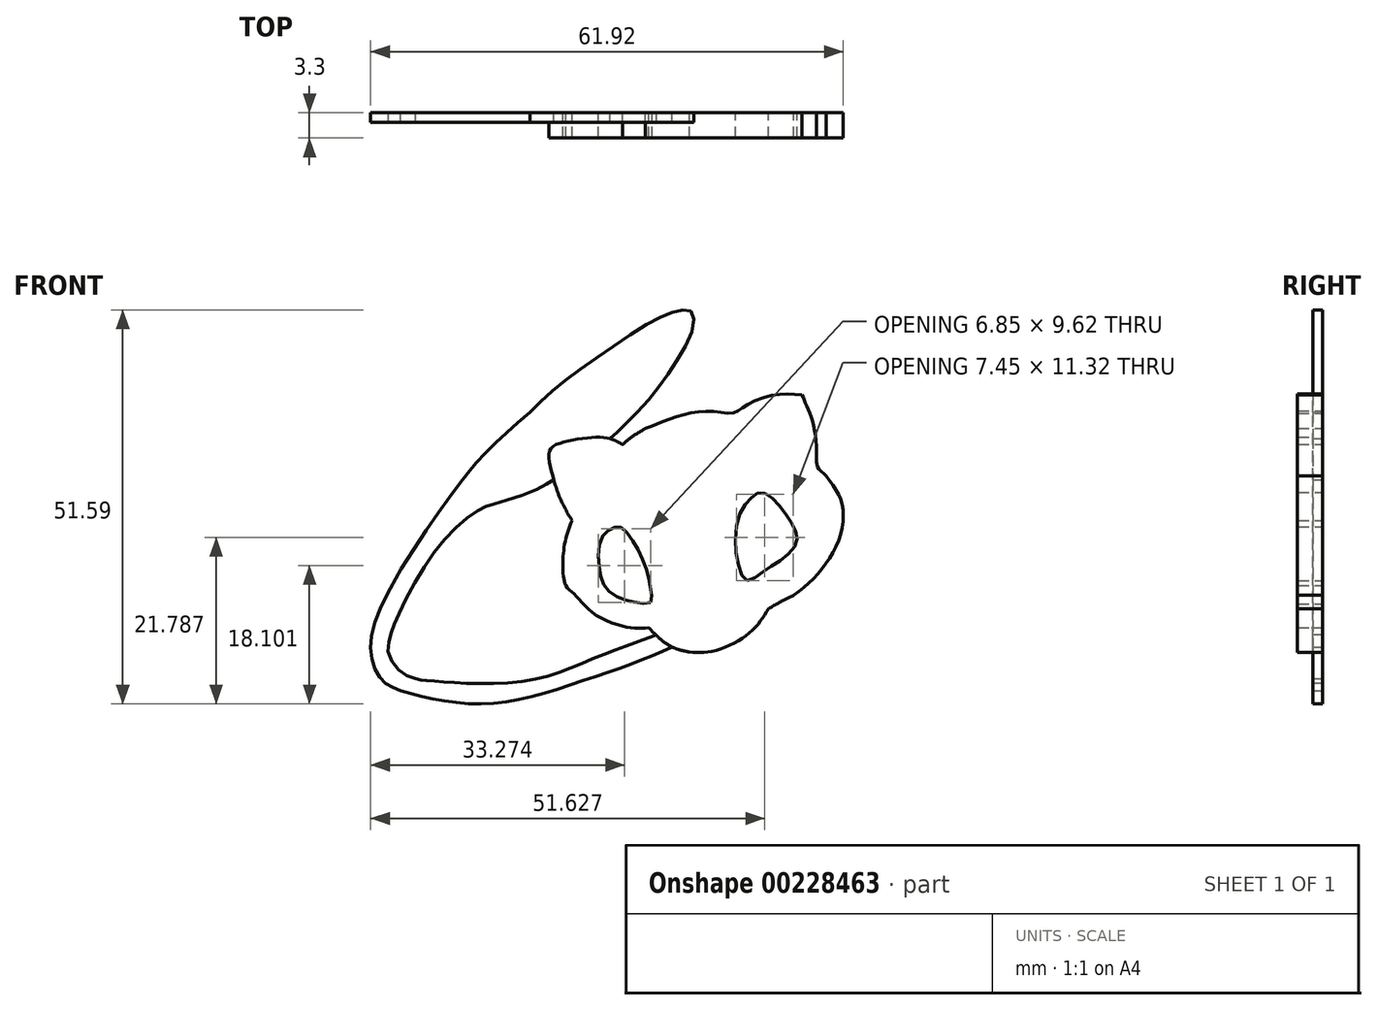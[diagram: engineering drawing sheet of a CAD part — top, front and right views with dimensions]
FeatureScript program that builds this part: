
annotation { "Feature Type Name" : "Feature", "Feature Type Description" : "" }
export const myFeature = defineFeature(function(context is Context, id is Id, definition is map)
    precondition{}
    {
        {
            var Q0;
            Q0=qCreatedBy(makeId("Front.planeOp"),FACE);
            var sketch = newSketch(context, id + "F0", { "sketchPlane" : qUnion([Q0])});
            skFitSpline(sketch, "E0", {"points": [v(-2.32, -20.69) * mm, v(0, -21.48) * mm, v(2.66, -21.63) * mm, v(5.5, -21.48) * mm, v(8.04, -20.05) * mm, v(10.01, -18.79) * mm], "startDerivative": vector(11.78, -4.97) * mm, "endDerivative": vector(10.2, 6.29) * mm});
            skFitSpline(sketch, "E1", {"points": [v(10.01, -18.79) * mm, v(12.15, -18.79) * mm, v(14.12, -18.79) * mm], "startDerivative": vector(4.23, 0) * mm, "endDerivative": vector(4, 0) * mm});
            skFitSpline(sketch, "E2", {"points": [v(14.12, -18.79) * mm, v(15.15, -21) * mm, v(16.42, -25.59) * mm, v(16.9, -29.38) * mm, v(17.13, -31.52) * mm], "startDerivative": vector(4.7, -9.02) * mm, "endDerivative": vector(1.16, -9.79) * mm});
            skFitSpline(sketch, "E3", {"points": [v(17.13, -31.52) * mm, v(17.74, -37.26) * mm, v(18.21, -42.48) * mm, v(19.24, -46.44) * mm, v(21.77, -48.9) * mm, v(26.22, -49.33) * mm, v(29.31, -47.38) * mm, v(29.8, -42.57) * mm, v(28.13, -36.9) * mm, v(26.29, -33.14) * mm, v(25.49, -31.52) * mm], "startDerivative": vector(5.72, -49.62) * mm, "endDerivative": vector(-10.88, 22.58) * mm});
            skFitSpline(sketch, "E4", {"points": [v(25.49, -31.52) * mm, v(24.09, -28.02) * mm, v(21.77, -21.94) * mm, v(20.2, -17.99) * mm, v(19.14, -16.04) * mm, v(18.38, -14.91) * mm], "startDerivative": vector(-6.12, 15.14) * mm, "endDerivative": vector(-5.8, 8.42) * mm});
            skFitSpline(sketch, "E5", {"points": [v(18.38, -14.91) * mm, v(18.1, -14.5) * mm], "startDerivative": vector(-0.29, 0.4) * mm, "endDerivative": vector(-0.29, 0.4) * mm});
            skFitSpline(sketch, "E6", {"points": [v(18.1, -14.5) * mm, v(18.1, -13.28) * mm, v(17.88, -10.97) * mm, v(16.93, -7.62) * mm, v(15.89, -5.67) * mm, v(14.88, -4.05) * mm], "startDerivative": vector(0.1, 7.63) * mm, "endDerivative": vector(-5.4, 8.63) * mm});
            skFitSpline(sketch, "E7", {"points": [v(14.88, -4.05) * mm, v(11.85, -1.17) * mm, v(8.44, 1.46) * mm, v(5.98, 3.57) * mm, v(4.78, 4.43) * mm, v(3.98, 5.1) * mm], "startDerivative": vector(-11.6, 11.83) * mm, "endDerivative": vector(-6.16, 5.39) * mm});
            skFitSpline(sketch, "E8", {"points": [v(3.98, 5.1) * mm, v(2.84, 6.42) * mm, v(1.91, 7.69) * mm, v(1.76, 8.46) * mm, v(1.71, 9.21) * mm, v(3.26, 9.37) * mm, v(5.98, 9.4) * mm, v(8.14, 9.24) * mm, v(9.13, 9.26) * mm, v(10.44, 8.7) * mm, v(11.35, 8.75) * mm, v(11.94, 9.66) * mm, v(12.76, 10.03) * mm, v(13.72, 10.65) * mm, v(13.36, 11.47) * mm, v(12.63, 11.98) * mm, v(12.7, 12.51) * mm], "startDerivative": vector(-14.72, 17.32) * mm, "endDerivative": vector(5.26, 13.9) * mm});
            skFitSpline(sketch, "E9", {"points": [v(12.7, 12.51) * mm, v(12.98, 13.02) * mm, v(12.4, 13.47) * mm, v(10.15, 14.02) * mm, v(7.27, 14.48) * mm, v(3.98, 14.64) * mm, v(2.38, 14.68) * mm], "startDerivative": vector(4.65, 5.52) * mm, "endDerivative": vector(-9, 0.23) * mm});
            skFitSpline(sketch, "E10", {"points": [v(2.38, 14.68) * mm, v(0, 14.68) * mm, v(-1.76, 14.68) * mm, v(-2.48, 15.55) * mm, v(-3.52, 16.92) * mm], "startDerivative": vector(-8.12, 0.34) * mm, "endDerivative": vector(-4.58, 5.53) * mm});
            skFitSpline(sketch, "E11", {"points": [v(-2.32, -20.69) * mm, v(-3.79, -21.48) * mm, v(-5.4, -21.63) * mm, v(-6.07, -21.63) * mm, v(-6.03, -22.06) * mm, v(-5.56, -23.59) * mm, v(-5.05, -24.67) * mm, v(-4.48, -25.94) * mm, v(-4.34, -26.18) * mm], "startDerivative": vector(-8.76, -5.85) * mm, "endDerivative": vector(1.87, -2.8) * mm});
            skFitSpline(sketch, "E12", {"points": [v(-4.34, -26.18) * mm, v(-3.52, -27.98) * mm, v(-2.32, -30.61) * mm, v(-1.07, -32.7) * mm, v(-0.47, -35.15) * mm, v(-0.51, -37.64) * mm, v(-1.62, -39.82) * mm, v(-3.52, -40.79) * mm, v(-6.34, -39.72) * mm, v(-9.34, -35.24) * mm, v(-10.78, -31.58) * mm, v(-12.12, -26.18) * mm, v(-12.77, -21.63) * mm, v(-13.04, -17.99) * mm, v(-12.9, -15.54) * mm], "startDerivative": vector(14.12, -29.7) * mm, "endDerivative": vector(3.47, 37.06) * mm});
            skFitSpline(sketch, "E13", {"points": [v(-12.9, -15.54) * mm, v(-11.8, -17.77) * mm, v(-9.63, -20.05) * mm, v(-8.07, -20.89) * mm, v(-6.86, -21.34) * mm, v(-6.07, -21.63) * mm], "startDerivative": vector(3.79, -9.41) * mm, "endDerivative": vector(5.46, -2.04) * mm});
            skFitSpline(sketch, "E14", {"points": [v(-12.9, -15.54) * mm, v(-12.9, -11.74) * mm, v(-11.8, -7.19) * mm, v(-10.92, -5.89) * mm, v(-10.92, -5.86) * mm], "startDerivative": vector(-0.49, 10.24) * mm, "endDerivative": vector(-0.26, 0.72) * mm});
            skFitSpline(sketch, "E15", {"points": [v(-10.92, -5.87) * mm, v(-10.92, -1.13) * mm, v(-10.92, 4.18) * mm, v(-11.8, 5.1) * mm, v(-15.41, 4.34) * mm, v(-19.88, 2.41) * mm, v(-22.2, 0.64) * mm, v(-22.89, 1.4) * mm, v(-24.04, 1.95) * mm, v(-24.12, 2.95) * mm, v(-24.81, 3.57) * mm, v(-22.35, 6.19) * mm, v(-19.03, 8.58) * mm, v(-17.2, 9.48) * mm], "startDerivative": vector(-1.12, 42.3) * mm, "endDerivative": vector(25.67, 11.36) * mm});
            skFitSpline(sketch, "E16", {"points": [v(-17.2, 9.48) * mm, v(-14.73, 9.48) * mm, v(-11, 10.84) * mm, v(-8.29, 13.04) * mm, v(-6.85, 15.16) * mm], "startDerivative": vector(10.44, -0.93) * mm, "endDerivative": vector(5.6, 9.42) * mm});
            skFitSpline(sketch, "E17", {"points": [v(-6.85, 15.16) * mm, v(-4.56, 16.43) * mm, v(-3.52, 16.92) * mm], "startDerivative": vector(4.16, 2.38) * mm, "endDerivative": vector(2.36, 1.05) * mm});
            skFitSpline(sketch, "E18", {"points": [v(-3.52, 16.92) * mm, v(-0.96, 19.09) * mm, v(1.19, 21.83) * mm, v(2.7, 25.14) * mm, v(2.89, 28.24) * mm, v(2.2, 30.33) * mm, v(0.71, 32.57) * mm], "startDerivative": vector(15.23, 11.78) * mm, "endDerivative": vector(-10.56, 14.43) * mm});
            skFitSpline(sketch, "E19", {"points": [v(0.71, 32.57) * mm, v(-0.4, 33.72) * mm, v(-0.53, 35.04) * mm, v(-0.9, 39) * mm, v(-1.85, 41.77) * mm, v(-2.44, 43.15) * mm], "startDerivative": vector(-7.97, 6.62) * mm, "endDerivative": vector(-3.3, 7.74) * mm});
            skFitSpline(sketch, "E20", {"points": [v(-2.44, 43.15) * mm, v(-5.96, 43.15) * mm, v(-9.92, 41.7) * mm, v(-11.39, 40.8) * mm, v(-14.05, 41) * mm, v(-17.62, 40.66) * mm, v(-20.71, 39.63) * mm, v(-22.98, 38.76) * mm], "startDerivative": vector(-21.66, 2.06) * mm, "endDerivative": vector(-17, -6.5) * mm});
            skFitSpline(sketch, "E21", {"points": [v(-22.98, 38.76) * mm, v(-24.87, 37.56) * mm, v(-25.95, 36.65) * mm], "startDerivative": vector(-3.66, -2.18) * mm, "endDerivative": vector(-2.23, -2.04) * mm});
            skFitSpline(sketch, "E22", {"points": [v(-25.95, 36.65) * mm, v(-27.6, 37.4) * mm, v(-30, 37.57) * mm, v(-33.8, 36.95) * mm, v(-35.53, 35.82) * mm, v(-35.25, 33.06) * mm, v(-34.2, 29.73) * mm, v(-32.6, 26.69) * mm], "startDerivative": vector(-13.7, 7.67) * mm, "endDerivative": vector(11, -18.84) * mm});
            skFitSpline(sketch, "E23", {"points": [v(-32.6, 26.69) * mm, v(-33.42, 24.25) * mm, v(-33.75, 21.83) * mm, v(-33.75, 19.77) * mm, v(-33.42, 18.22) * mm], "startDerivative": vector(-3.32, -8.47) * mm, "endDerivative": vector(2.23, -4.7) * mm});
            skFitSpline(sketch, "E24", {"points": [v(-17.2, 9.48) * mm, v(-19.5, 10.14) * mm, v(-21.6, 11.71) * mm, v(-22.5, 12.66) * mm], "startDerivative": vector(-6.2, 1.22) * mm, "endDerivative": vector(-2.9, 3.33) * mm});
            skFitSpline(sketch, "E25", {"points": [v(-22.5, 12.66) * mm, v(-24.99, 12.66) * mm, v(-29.66, 14.48) * mm, v(-32.24, 17) * mm, v(-33.42, 18.22) * mm], "startDerivative": vector(-10.22, -1.06) * mm, "endDerivative": vector(-5.21, 8.6) * mm});
            skFitSpline(sketch, "E26", {"points": [v(17.59, -9.61) * mm, v(19.29, -7.66) * mm, v(23.64, -4.88) * mm, v(28.4, -1.83) * mm, v(33.2, 1.85) * mm, v(38.49, 6.47) * mm, v(41.31, 9.79) * mm, v(43.06, 12.66) * mm], "startDerivative": vector(13.38, 18.51) * mm, "endDerivative": vector(13.65, 24.07) * mm});
            skFitSpline(sketch, "E27", {"points": [v(43.06, 12.66) * mm, v(43.71, 15.42) * mm, v(43.06, 18.22) * mm, v(39.59, 21.32) * mm, v(33.2, 22.4) * mm, v(25.39, 22.35) * mm, v(17.88, 21.9) * mm, v(12.32, 21.17) * mm], "startDerivative": vector(8.03, 25.04) * mm, "endDerivative": vector(-36.28, -5.52) * mm});
            skFitSpline(sketch, "E28", {"points": [v(12.32, 21.17) * mm, v(6.63, 20.02) * mm, v(0, 18.22) * mm, v(-3.52, 16.92) * mm], "startDerivative": vector(-15.79, -3.65) * mm, "endDerivative": vector(-10.95, -7.5) * mm});
            skFitSpline(sketch, "E29", {"points": [v(15.21, -4.6) * mm, v(18, -4.6) * mm, v(23.06, -2.1) * mm, v(30.27, 3.2) * mm, v(38.18, 10.01) * mm, v(41.35, 14.52) * mm, v(41.35, 17.21) * mm, v(39.45, 19.04) * mm, v(32.72, 20.14) * mm, v(24.1, 19.99) * mm, v(15.21, 19.2) * mm, v(6.44, 17.45) * mm, v(0, 15.63) * mm, v(-1.76, 14.68) * mm], "startDerivative": vector(49.5, -6.25) * mm, "endDerivative": vector(-32.18, -20.9) * mm});
            skFitSpline(sketch, "E30", {"points": [v(-22.26, 15.98) * mm, v(-24.13, 15.98) * mm, v(-26.1, 16.49) * mm, v(-27.98, 17.68) * mm, v(-28.8, 19.41) * mm, v(-29.12, 22.25) * mm, v(-28.52, 24.72) * mm, v(-27.34, 25.68) * mm, v(-26.24, 25.82) * mm, v(-24.91, 24.5) * mm, v(-23.54, 22.07) * mm, v(-22.58, 19.46) * mm, v(-22.26, 17.5) * mm, v(-22.26, 15.98) * mm]});
            skFitSpline(sketch, "E31", {"points": [v(-9.64, 18.82) * mm, v(-10.6, 20.33) * mm, v(-11.2, 23.94) * mm, v(-10.46, 27.92) * mm, v(-9.04, 29.7) * mm, v(-7.9, 30.39) * mm, v(-6.53, 29.75) * mm, v(-4.93, 27.97) * mm, v(-3.5, 25.82) * mm, v(-3.1, 24.26) * mm, v(-3.92, 22.66) * mm, v(-5.93, 21.06) * mm, v(-7.85, 19.78) * mm, v(-9.64, 18.82) * mm]});
            skFitSpline(sketch, "E32", {"points": [v(-19.5, 10.14) * mm, v(-25.11, 7.8) * mm, v(-32.9, 5.15) * mm, v(-41.27, 2.93) * mm, v(-48.85, 3) * mm, v(-55.07, 4.43) * mm], "startDerivative": vector(-29.49, -12.97) * mm, "endDerivative": vector(-32.45, 8.89) * mm});
            skFitSpline(sketch, "E33", {"points": [v(-55.07, 4.43) * mm, v(-57.26, 5.61) * mm, v(-58.78, 8.58) * mm, v(-57.93, 14.7) * mm, v(-49.08, 29.15) * mm, v(-44.2, 35.25) * mm, v(-38.1, 40.86) * mm], "startDerivative": vector(-24, 8.54) * mm, "endDerivative": vector(35.7, 31.15) * mm});
            skFitSpline(sketch, "E34", {"points": [v(-38.1, 40.86) * mm, v(-34.31, 44.39) * mm, v(-28.1, 48.87) * mm, v(-21.6, 53.05) * mm, v(-18.6, 54.14) * mm, v(-16.99, 54.1) * mm, v(-16.73, 52) * mm, v(-19.03, 47.36) * mm, v(-22.15, 42.98) * mm, v(-25.96, 38.96) * mm, v(-27.6, 37.4) * mm], "startDerivative": vector(32.13, 32) * mm, "endDerivative": vector(-19.9, -18.7) * mm});
            skFitSpline(sketch, "E35", {"points": [v(-34.98, 32.05) * mm, v(-37, 30.87) * mm, v(-42.5, 28.96) * mm, v(-44.35, 28.35) * mm, v(-47.78, 25.82) * mm, v(-52.27, 20.1) * mm, v(-55.58, 13.8) * mm, v(-56.31, 11.71) * mm, v(-56.65, 9.42) * mm, v(-55.07, 6.95) * mm, v(-53.05, 6.02) * mm], "startDerivative": vector(-19.73, -13.88) * mm, "endDerivative": vector(26.74, -3.56) * mm});
            skFitSpline(sketch, "E36", {"points": [v(-53.05, 6.02) * mm, v(-51.46, 5.73) * mm, v(-46.35, 5.4) * mm, v(-36.86, 6.02) * mm, v(-29.96, 8.58) * mm, v(-24.04, 10.8) * mm, v(-21.6, 11.71) * mm], "startDerivative": vector(13.62, -6.94) * mm, "endDerivative": vector(17.92, 6.78) * mm});
            skSolve(sketch);
        }
        {
            var Q0;
            {var subQ0=sQuery(id+"F0.wireOp",EDGE,"E32");Q0=makeQuery(id+"F0.imprint","IMPRINT",FACE,{"disambiguationData":[TD([[makeQuery(id+"F0.imprint","IMPRINT",EDGE,{"derivedFrom":subQ0}),-1.0]])]});}
            extrude(context, id + "F1", {"entities" : qUnion([Q0]), "depth" : 1.27 * mm});
        }
        {
            var Q0;
            {var subQ9=sQuery(id+"F0.wireOp",EDGE,"E16");Q0=makeQuery(id+"F0.imprint","IMPRINT",FACE,{"disambiguationData":[TD([[makeQuery(id+"F0.imprint","IMPRINT",EDGE,{"derivedFrom":subQ9}),1.0]])]});}
            extrude(context, id + "F2", {"entities" : qUnion([Q0]), "operationType" : NewBodyOperationType.ADD, "depth" : 3.3 * mm});
        }
    });
